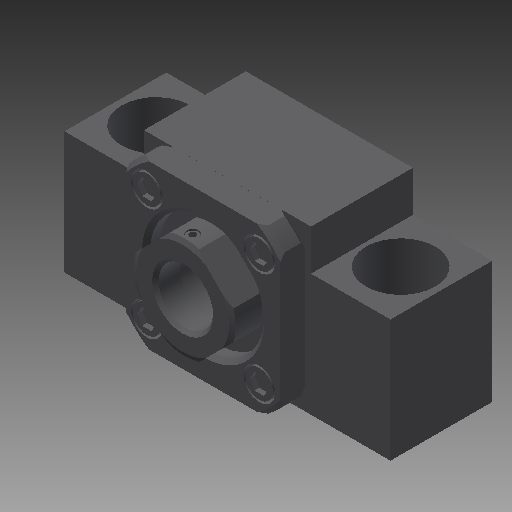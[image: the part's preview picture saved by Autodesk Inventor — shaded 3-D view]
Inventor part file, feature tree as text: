
AUTODESK INVENTOR PART (.ipt)
format: ipt  version: 2018 (Build 220112000, 112)  size: 393,728 bytes
history: native  units: mm
features: sketch x24, other x14, revolve x12, extrude x9, hole x3, pattern_linear x3, thread x1
ambient origin geometry x8: Origin, YZ Plane, XZ Plane, XY Plane, X Axis, Y Axis, Z Axis, Center Point
bodies: Solid1 (feature_tree)
feature tree (66):
  extrude  "Extrusion1"  Depth=2.5mm TaperAngle=0.0deg
  hole  "Hole1"  [1 undecoded]
  extrude  "Extrusion2"  TaperAngle=360.0deg  [1 undecoded]
  revolve  "Revolution1"  Angle=360.0deg
  extrude  "Extrusion3"  TaperAngle=360.0deg  [1 undecoded]
  extrude  "Extrusion4"  Depth=20.0mm
  revolve  "Revolution2"  [1 undecoded]
  hole  "Hole5"  [1 undecoded]
  revolve  "Revolution3"  Angle=360.0deg
  thread  "Thread1"  [1 undecoded]
  revolve  "Revolution4"  Angle=360.0deg
  revolve  "Revolution5"  [1 undecoded]
  pattern_linear  "Rectangular Pattern1"  Count1=8  [1 undecoded]
  revolve  "Revolution6"  [1 undecoded]
  pattern_linear  "Rectangular Pattern2"  Count1=4  [1 undecoded]
  extrude  "Extrusion5"  Depth=10.0mm
  pattern_linear  "Rectangular Pattern3"  Count1=2  [1 undecoded]
  revolve  "Revolution7"  [1 undecoded]
  revolve  "Revolution8"  [1 undecoded]
  extrude  "Extrusion6"  [1 undecoded]
  revolve  "Revolution9"  [1 undecoded]
  revolve  "Revolution10"  [1 undecoded]
  extrude  "Extrusion7"  [1 undecoded]
  extrude  "Extrusion8"  [1 undecoded]
  revolve  "Revolution11"  [1 undecoded]
  revolve  "Revolution12"  [1 undecoded]
  extrude  "Extrusion9"  [1 undecoded]
  other  "unit_XY"
  other  "unit_YZ"
  other  "unit_ZX"
  other  "unit_X"
  other  "unit_Y"
  other  "unit_Z"
  other  "unit_Center"
  other  "unit_collar_XY"
  other  "unit_collar_YZ"
  other  "unit_collar_ZX"
  other  "unit_collar_X"
  other  "unit_collar_Y"
  other  "unit_collar_Z"
  other  "unit_collar_Center"
  sketch  "Sketch_1"  dims[d0=25.0mm d1=0.0mm]
  sketch  "Sketch2"  dims[d2=11.0mm d3=6.0mm d4=17.0mm d5=15.0mm d6=90.0deg d7=38.0mm d8=0.0mm d30=2.5mm d31=0.0mm]
  sketch  "Sketch_10"  dims[d32=360.0deg d33=8.5mm d34=0.0mm]
  sketch  "Sketch_13"  dims[d49=360.0deg d50=20.0mm d52=27.577164mm d53=20.0mm d55=27.577164mm]
  sketch  "Sketch_11"  dims[d35=3.5mm d36=0.0mm d37=360.0deg]
  sketch  "Sketch_12"  dims[d46=6.876mm d47=0.0mm d48=360.0deg]
  sketch  "Sketch_14"  dims[d56=360.0deg d57=20.0mm d59=27.577164mm d60=20.0mm d62=27.577164mm]
  sketch  "Sketch11"  dims[d38=15.0mm d39=6.0mm d40=19.5mm d41=6.0mm d42=90.0deg d43=30.0mm d44=0.0mm d45=360.0deg]
  sketch  "Sketch_16"  dims[d63=1.2mm d64=0.0mm d65=20.0mm d67=27.577164mm d68=20.0mm d70=27.577164mm]
  sketch  "Sketch_17"  dims[d71=360.0deg d72=360.0deg d73=1.2mm d74=0.0mm]
  sketch  "Sketch_18"  dims[d75=360.0deg d76=360.0deg]
  sketch  "Sketch_20"  dims[d77=16.0mm d78=0.0mm d79=6.0mm d80=0.0mm]
  sketch  "Sketch_22"  dims[d81=360.0deg]
  sketch  "Sketch_24"  dims[d82=360.0deg]
  sketch  "Sketch_25"  dims[d83=0.01mm d84=0.0mm]
  sketch  "Sketch_26"  dims[d85=0.0mm]
  sketch  "Sketch_28"  dims[d91=28.0mm]
  sketch  "Sketch_29"  dims[d92=38.0mm]
  sketch  "Sketch_33"  dims[d101=0.0mm d102=90.0deg d103=15.0mm d104=17.0mm d105=38.0mm d106=11.0mm d107=10.0mm d108=10.0mm]
  sketch  "Sketch_27"  dims[d86=0.0mm d87=80.0mm]
  sketch  "Sketch_30"  dims[d93=38.0mm d94=40.0mm]
  sketch  "Sketch_31"  dims[d95=40.0mm d97=10.0mm d98=20.0mm]
  sketch  "Sketch_32"  dims[d99=6.0mm]
  sketch  "Sketch27"  dims[d88=40.0mm d90=41.0mm]
  hole  "Hole6"  [1 undecoded]
note: 22 required parameter values undecoded (feature->parameter linkage not recoverable at this tier; creation-order binding heuristic only, values carry confidence <= 0.55)